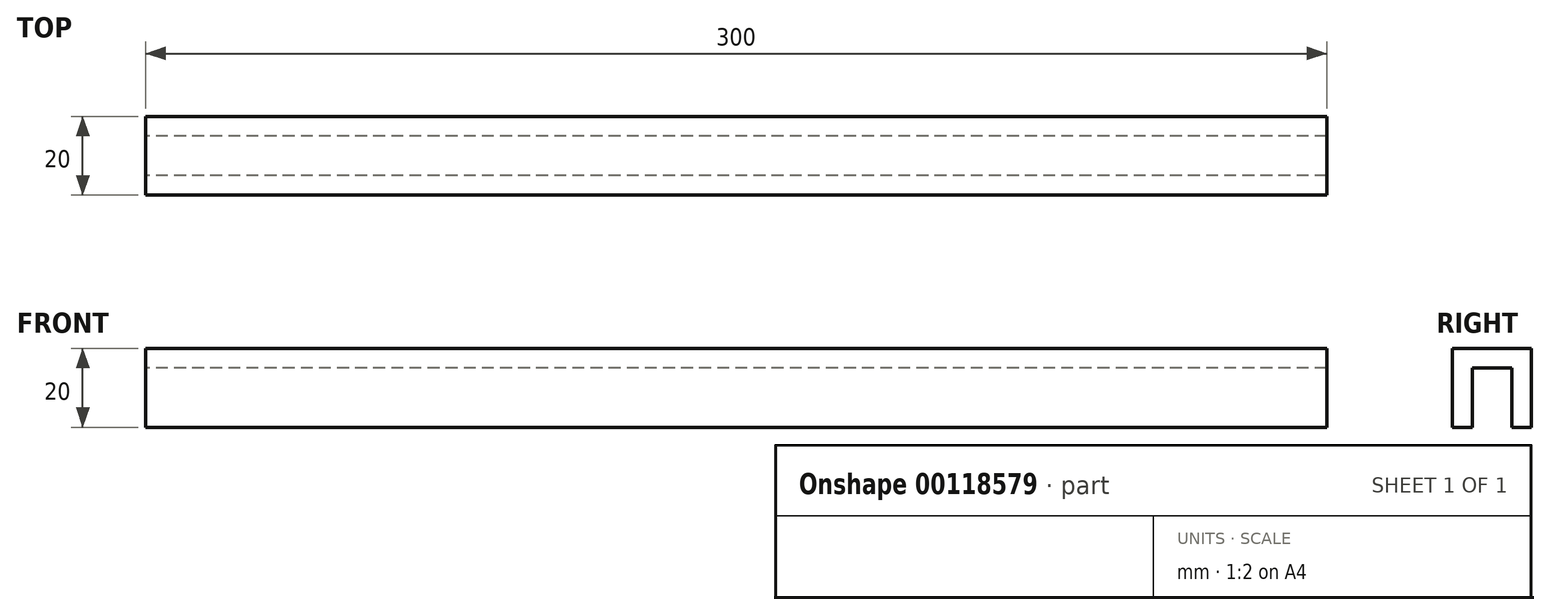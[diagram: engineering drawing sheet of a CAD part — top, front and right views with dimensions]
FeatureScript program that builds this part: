
annotation { "Feature Type Name" : "Feature", "Feature Type Description" : "" }
export const myFeature = defineFeature(function(context is Context, id is Id, definition is map)
    precondition{}
    {
        {
            var Q0;
            Q0=qCreatedBy(makeId("Right.planeOp"),FACE);
            var sketch = newSketch(context, id + "F0", { "sketchPlane" : qUnion([Q0])});
            skLineSegment(sketch, "E0.bottom", {"start": v(10, 10) * mm, "end": v(-10, 10) * mm});
            skLineSegment(sketch, "E0.top", {"start": v(10, -10) * mm, "end": v(5, -10) * mm});
            skLineSegment(sketch, "E0.left", {"start": v(10, 10) * mm, "end": v(10, -10) * mm});
            skLineSegment(sketch, "E0.right", {"start": v(-10, 10) * mm, "end": v(-10, -10) * mm});
            skPoint(sketch, "E0.middle", {"position": v(0, 0) * mm});
            skLineSegment(sketch, "E1", {"start": v(5, -10) * mm, "end": v(5, 5) * mm});
            skLineSegment(sketch, "E2", {"start": v(5, 5) * mm, "end": v(-5, 5) * mm});
            skLineSegment(sketch, "E3", {"start": v(-5, 5) * mm, "end": v(-5, -10) * mm});
            skLineSegment(sketch, "E4.trimOffspring", {"start": v(-5, -10) * mm, "end": v(-10, -10) * mm});
            skSolve(sketch);
        }
        {
            var Q0;
            Q0 = qSketchRegion(id + "F0", true);
            extrude(context, id + "F1", {"entities" : qUnion([Q0]), "depth" : 300 * mm});
        }
    });
